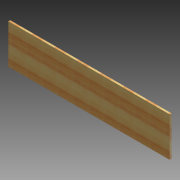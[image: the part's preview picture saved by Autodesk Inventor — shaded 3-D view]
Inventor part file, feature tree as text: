
AUTODESK INVENTOR PART (.ipt)
format: ipt  version: 2012 (Build 160160000, 160)  size: 142,336 bytes
history: native  units: in
note: dims shown in document units (in); Inventor stores cm internally (conversion verified against a paired STEP export)
features: extrude x1, fillet x1, sketch x1
ambient origin geometry x8: Origin, YZ Plane, XZ Plane, XY Plane, X Axis, Y Axis, Z Axis, Center Point
bodies: Solid1 (feature_tree)
feature tree (3):
  extrude  "Extrusion1"  Depth=9.0in
  fillet  "Fillet1"  Radius=0.4375in
  sketch  "Sketch1"  dims[d0=37.0in d1=9.0in d2=0.4375in d3=0.0in d4=6.0in d5=18.25in d6=5.0in d7=5.0in d9=0.25in d10=0.5in d18=3.937in d19=3.937in d20=0.25in d21=0.25in d22=0.25in d23=0.25in d24=1.5748in d26=360.0deg d28=1.9685in d30=5.0in d31=0.3937in d33=1.0in]
